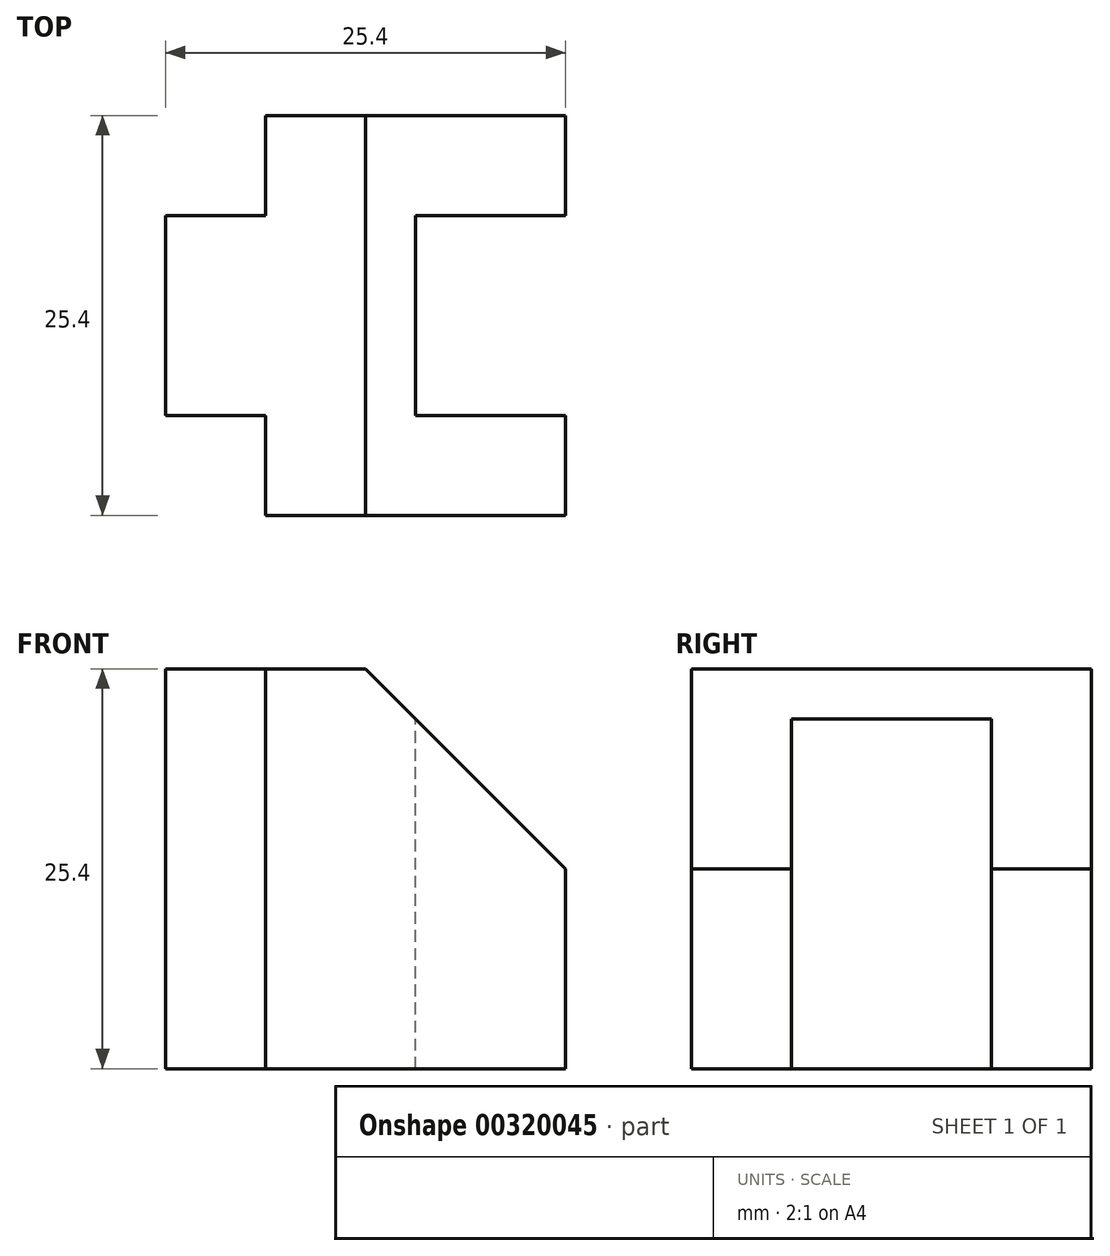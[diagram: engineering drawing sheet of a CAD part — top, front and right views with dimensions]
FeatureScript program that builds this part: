
annotation { "Feature Type Name" : "Feature", "Feature Type Description" : "" }
export const myFeature = defineFeature(function(context is Context, id is Id, definition is map)
    precondition{}
    {
        {
            var Q0;
            Q0=qCreatedBy(makeId("Front.planeOp"),FACE);
            var sketch = newSketch(context, id + "F0", { "sketchPlane" : qUnion([Q0])});
            skLineSegment(sketch, "E0", {"start": v(0, 0) * mm, "end": v(0, 25.4) * mm});
            skLineSegment(sketch, "E1", {"start": v(0, 25.4) * mm, "end": v(25.4, 25.4) * mm});
            skLineSegment(sketch, "E2", {"start": v(25.4, 25.4) * mm, "end": v(25.4, 0) * mm});
            skLineSegment(sketch, "E3", {"start": v(25.4, 0) * mm, "end": v(0, 0) * mm});
            skSolve(sketch);
        }
        {
            var Q0;
            Q0 = qSketchRegion(id + "F0", true);
            extrude(context, id + "F1", {"entities" : qUnion([Q0]), "depth" : 25.4 * mm});
        }
        {
            var Q0;
            Q0=makeQuery(id+"F1.opExtrude","SWEPT_FACE",FACE,{"disambiguationData":[OSD([sQuery(id+"F0.wireOp",EDGE,"E1")])]});
            var sketch = newSketch(context, id + "F2", { "sketchPlane" : qUnion([Q0])});
            skLineSegment(sketch, "E4", {"start": v(0, 0) * mm, "end": v(6.35, 0) * mm});
            skLineSegment(sketch, "E5", {"start": v(6.35, 0) * mm, "end": v(6.35, -6.35) * mm});
            skLineSegment(sketch, "E6", {"start": v(6.35, -6.35) * mm, "end": v(0, -6.35) * mm});
            skLineSegment(sketch, "E7", {"start": v(0, 0) * mm, "end": v(0, -6.35) * mm});
            skLineSegment(sketch, "E8", {"start": v(0, -25.4) * mm, "end": v(0, -19.05) * mm});
            skLineSegment(sketch, "E9", {"start": v(0, -19.05) * mm, "end": v(6.35, -19.05) * mm});
            skLineSegment(sketch, "E10", {"start": v(6.35, -19.05) * mm, "end": v(6.35, -25.4) * mm});
            skLineSegment(sketch, "E11", {"start": v(6.35, -25.4) * mm, "end": v(0, -25.4) * mm});
            skLineSegment(sketch, "E12", {"start": v(25.4, 0) * mm, "end": v(25.4, -6.35) * mm});
            skLineSegment(sketch, "E13", {"start": v(25.4, -6.35) * mm, "end": v(25.4, -19.05) * mm});
            skLineSegment(sketch, "E14", {"start": v(25.4, -19.05) * mm, "end": v(15.88, -19.05) * mm});
            skLineSegment(sketch, "E15", {"start": v(15.88, -19.05) * mm, "end": v(15.88, -6.35) * mm});
            skLineSegment(sketch, "E16", {"start": v(15.88, -6.35) * mm, "end": v(25.4, -6.35) * mm});
            skSolve(sketch);
        }
        {
            var Q0;
            Q0 = qSketchRegion(id + "F2", true);
            extrude(context, id + "F3", {"entities" : qUnion([Q0]), "operationType" : NewBodyOperationType.REMOVE, "oppositeDirection" : true, "depth" : 25.4 * mm});
        }
        {
            var Q0;
            Q0=makeQuery(id+"F1.opExtrude","CAP_FACE",FACE,{"disambiguationData":[OSD([sQuery(id+"F0.wireOp",EDGE,"E0"),sQuery(id+"F0.wireOp",EDGE,"E1"),sQuery(id+"F0.wireOp",EDGE,"E2"),sQuery(id+"F0.wireOp",EDGE,"E3")])],"isStart":false});
            var sketch = newSketch(context, id + "F4", { "sketchPlane" : qUnion([Q0])});
            skLineSegment(sketch, "E17", {"start": v(6.35, 25.4) * mm, "end": v(12.7, 25.4) * mm});
            skLineSegment(sketch, "E18", {"start": v(25.4, 12.7) * mm, "end": v(12.7, 25.4) * mm});
            skLineSegment(sketch, "E19", {"start": v(12.7, 25.4) * mm, "end": v(25.4, 25.4) * mm});
            skLineSegment(sketch, "E20", {"start": v(25.4, 25.4) * mm, "end": v(25.4, 12.7) * mm});
            skSolve(sketch);
        }
        {
            var Q0;
            Q0 = qSketchRegion(id + "F4", true);
            extrude(context, id + "F5", {"entities" : qUnion([Q0]), "operationType" : NewBodyOperationType.REMOVE, "oppositeDirection" : true, "depth" : 76.2 * mm});
        }
    });
